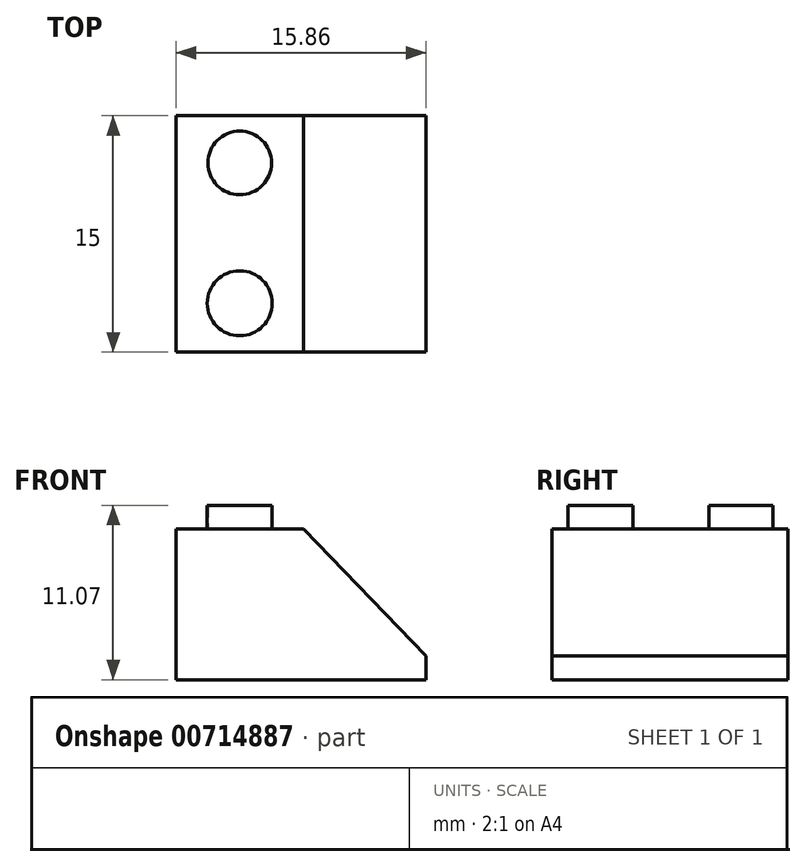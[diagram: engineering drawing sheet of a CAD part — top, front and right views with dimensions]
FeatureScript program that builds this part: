
annotation { "Feature Type Name" : "Feature", "Feature Type Description" : "" }
export const myFeature = defineFeature(function(context is Context, id is Id, definition is map)
    precondition{}
    {
        {
            var Q0;
            Q0=qCreatedBy(makeId("Front.planeOp"),FACE);
            var sketch = newSketch(context, id + "F0", { "sketchPlane" : qUnion([Q0])});
            skLineSegment(sketch, "E0", {"start": v(0, 0) * mm, "end": v(0, 9.57) * mm});
            skLineSegment(sketch, "E1", {"start": v(0, 9.57) * mm, "end": v(8.08, 9.57) * mm});
            skLineSegment(sketch, "E2", {"start": v(0, 0) * mm, "end": v(15.86, 0) * mm});
            skLineSegment(sketch, "E3", {"start": v(15.86, 0) * mm, "end": v(15.86, 1.53) * mm});
            skLineSegment(sketch, "E4", {"start": v(15.86, 1.53) * mm, "end": v(8.08, 9.57) * mm});
            skSolve(sketch);
        }
        {
            var Q0;
            Q0 = qSketchRegion(id + "F0", true);
            extrude(context, id + "F1", {"entities" : qUnion([Q0]), "depth" : 15 * mm, "offsetDistance" : 25 * mm});
        }
        {
            var Q0;
            Q0=makeQuery(id+"F1.opExtrude","SWEPT_FACE",FACE,{"disambiguationData":[OSD([sQuery(id+"F0.wireOp",EDGE,"E1")])]});
            var sketch = newSketch(context, id + "F2", { "sketchPlane" : qUnion([Q0])});
            skCircle(sketch, "E5", {"center": v(4.04, -11.9) * mm, "radius": 2.06 * mm});
            skCircle(sketch, "E6", {"center": v(4.04, -3) * mm, "radius": 2.02 * mm});
            skSolve(sketch);
        }
        {
            var Q0;
            Q0 = qSketchRegion(id + "F2", true);
            extrude(context, id + "F3", {"entities" : qUnion([Q0]), "operationType" : NewBodyOperationType.ADD, "depth" : 1.5 * mm, "offsetDistance" : 25 * mm});
        }
    });
